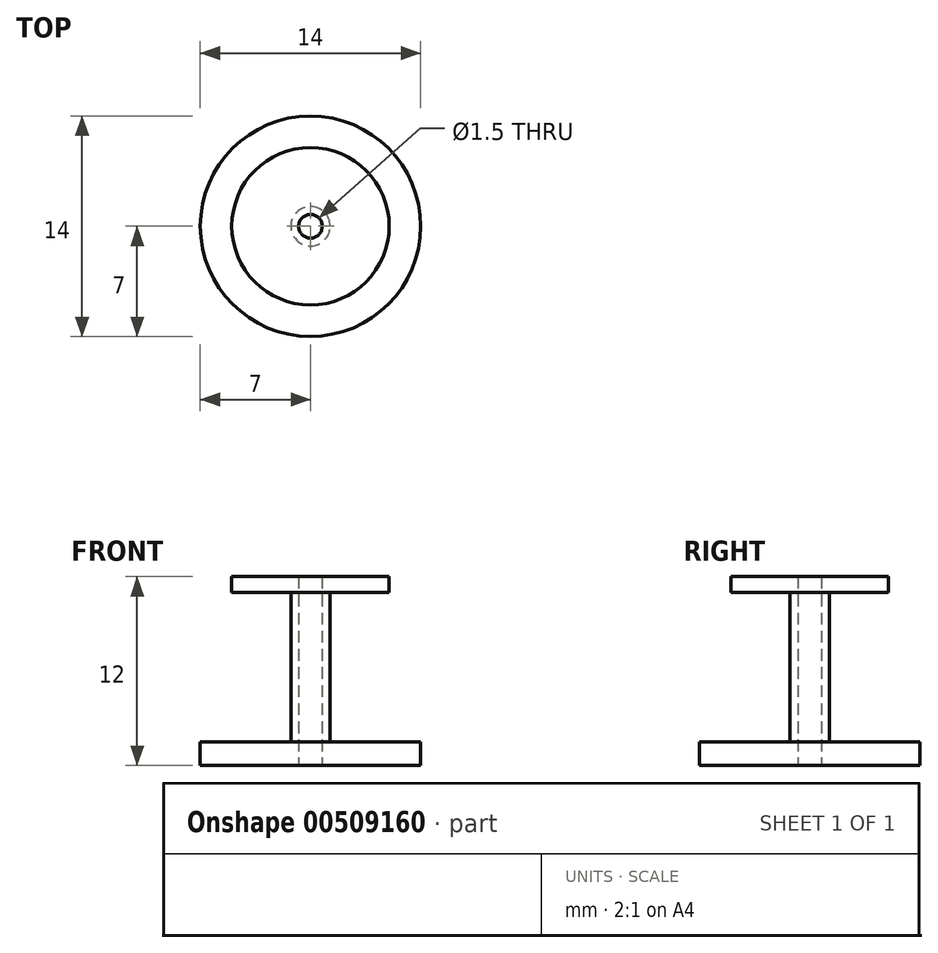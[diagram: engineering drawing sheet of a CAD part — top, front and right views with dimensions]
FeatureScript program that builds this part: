
annotation { "Feature Type Name" : "Feature", "Feature Type Description" : "" }
export const myFeature = defineFeature(function(context is Context, id is Id, definition is map)
    precondition{}
    {
        {
            var Q0;
            Q0=qCreatedBy(makeId("Top.planeOp"),FACE);
            cPlane(context, id + "F0", {"entities" : qUnion([Q0]), "cplaneType" : CPlaneType.OFFSET, "offset" : 7 * mm, "width" : 150 * mm, "height" : 150 * mm});
        }
        {
            var Q0;
            Q0=qCreatedBy(id+"F0.planeOp",FACE);
            var sketch = newSketch(context, id + "F1", { "sketchPlane" : qUnion([Q0])});
            skCircle(sketch, "E0", {"center": v(0, 0) * mm, "radius": 7 * mm});
            skCircle(sketch, "E1", {"center": v(0, 0) * mm, "radius": 0.75 * mm});
            skSolve(sketch);
        }
        {
            var Q0;
            Q0=makeQuery(id+"F1.imprint","IMPRINT",FACE,{"disambiguationData":[TD([[makeQuery(id+"F1.imprint","IMPRINT",EDGE,{"derivedFrom":sQuery(id+"F1.wireOp",EDGE,"E0")}),1.0]])]});
            extrude(context, id + "F2", {"entities" : qUnion([Q0]), "depth" : 1.5 * mm});
        }
        {
            var Q0;
            Q0=makeQuery(id+"F2.opExtrude","CAP_FACE",FACE,{"disambiguationData":[OSD([sQuery(id+"F1.wireOp",EDGE,"E0")])],"isStart":false});
            var sketch = newSketch(context, id + "F3", { "sketchPlane" : qUnion([Q0])});
            skCircle(sketch, "E2", {"center": v(0, 0) * mm, "radius": 1.25 * mm});
            skSolve(sketch);
        }
        {
            var Q0;
            Q0=makeQuery(id+"F3.imprint","IMPRINT",FACE,{"disambiguationData":[TD([[makeQuery(id+"F3.imprint","IMPRINT",EDGE,{"derivedFrom":sQuery(id+"F3.wireOp",EDGE,"E2")}),1.0]])]});
            extrude(context, id + "F4", {"entities" : qUnion([Q0]), "operationType" : NewBodyOperationType.ADD, "depth" : 9.5 * mm});
        }
        {
            var Q0;
            Q0=makeQuery(id+"F4.opExtrude","CAP_FACE",FACE,{"disambiguationData":[OSD([sQuery(id+"F3.wireOp",EDGE,"E2")])],"isStart":false});
            var sketch = newSketch(context, id + "F5", { "sketchPlane" : qUnion([Q0])});
            skCircle(sketch, "E3", {"center": v(0, 0) * mm, "radius": 5 * mm});
            skSolve(sketch);
        }
        {
            var Q0;
            Q0=makeQuery(id+"F5.imprint","IMPRINT",FACE,{"disambiguationData":[TD([[makeQuery(id+"F5.imprint","IMPRINT",EDGE,{"derivedFrom":sQuery(id+"F5.wireOp",EDGE,"E3")}),1.0]])]});
            var Q1;
            Q1=makeQuery(id+"F5.imprint","IMPRINT",FACE,{"disambiguationData":[TD([[makeQuery(id+"F5.imprint","IMPRINT",EDGE,{"derivedFrom":makeQuery(id+"F4.opExtrude","CAP_EDGE",EDGE,{"disambiguationData":[OSD([sQuery(id+"F3.wireOp",EDGE,"E2")])],"isStart":false})}),1.0]])]});
            extrude(context, id + "F6", {"entities" : qUnion([Q0, Q1]), "operationType" : NewBodyOperationType.ADD, "depth" : 1 * mm});
        }
    });
